SOLIDWORKS PART (.sldprt)
format: sldprt  version: not decoded by parser v0  size: 133,632 bytes
history: native  units: mm
features: sketch x4, plane x3, material x1, revolve x1, extrude x1, cut_extrude x1 (+11 scaffold rows collapsed)
feature tree (22):
  scaffold x11  (default folders/planes/origin — collapsed)
  material  "Matériau <non spécifié>"
  plane  "Plan de face"
  plane  "Plan de dessus"
  plane  "Plan de droite"
  sketch  "Esquisse1"  dims[D1=8.0mm D2=8.5mm]
  revolve  "Révolution1"  Angle=360deg
  sketch  "Esquisse2"  dims[D1=0.5mm]
  sketch  "Esquisse3"  dims[D1=3.0mm]
  extrude  "Extrusion2"  Depth=19mm
  sketch  "Esquisse4"  dims[D1=5.0mm]
  cut_extrude  "Extrusion4"  [1 undecoded]
decode coverage: 6 of 7 modeling features carry decoded parameters
note: 1 parameter value undecoded
note: suppression state not decoded; provenance and decode notes live in map.json
